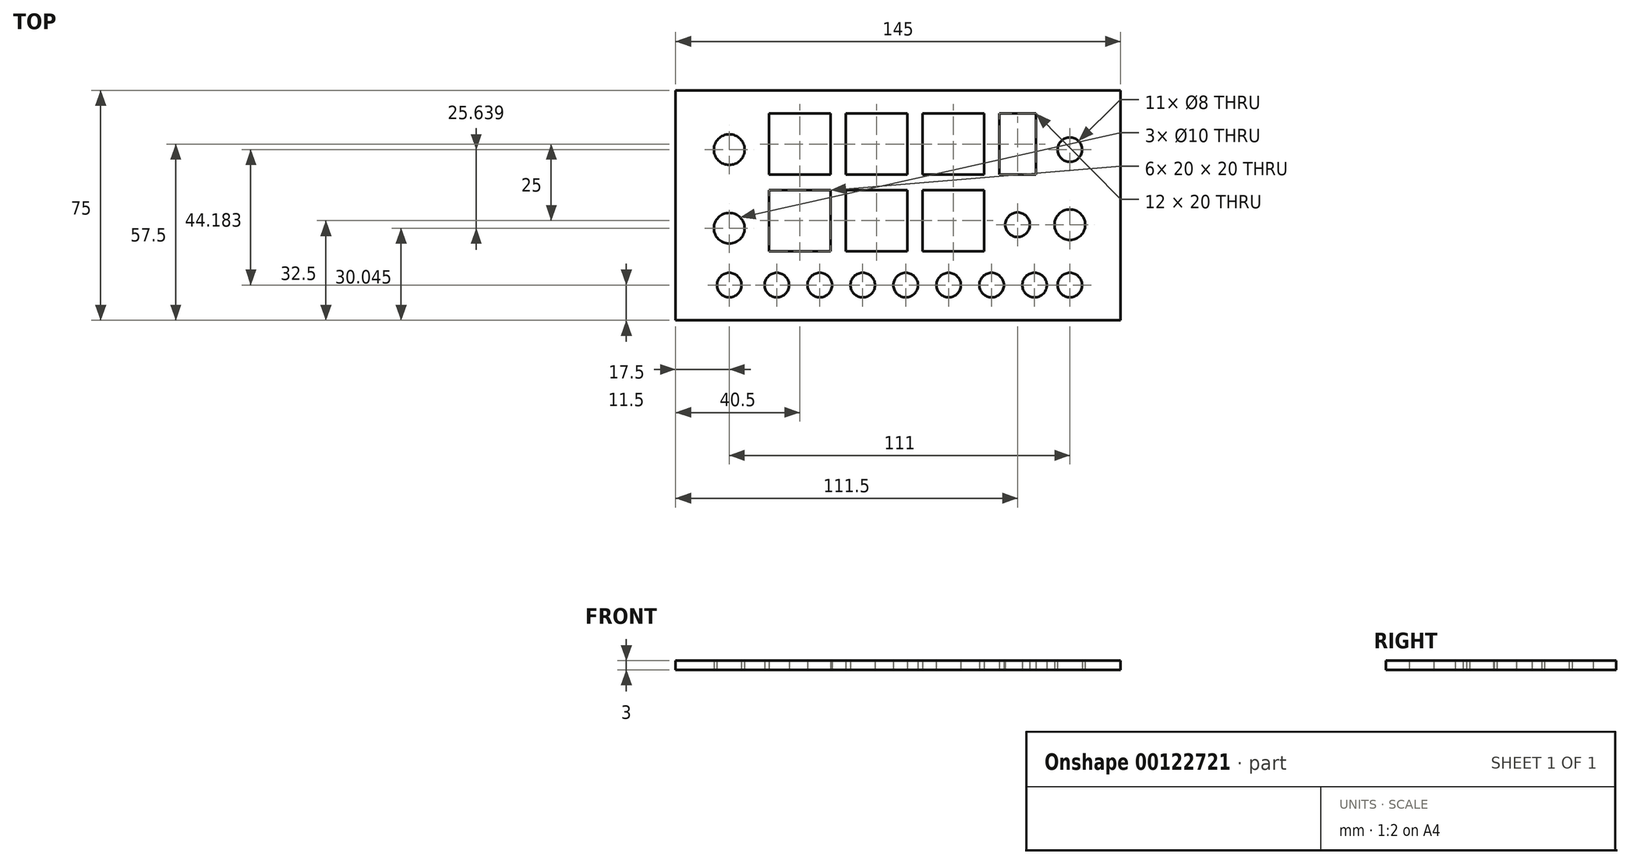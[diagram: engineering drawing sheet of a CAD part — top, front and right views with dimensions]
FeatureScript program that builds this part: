
annotation { "Feature Type Name" : "Feature", "Feature Type Description" : "" }
export const myFeature = defineFeature(function(context is Context, id is Id, definition is map)
    precondition{}
    {
        {
            var Q0;
            Q0=qCreatedBy(makeId("Top.planeOp"),FACE);
            var sketch = newSketch(context, id + "F0", { "sketchPlane" : qUnion([Q0])});
            skLineSegment(sketch, "E0.bottom", {"start": v(0, 0) * mm, "end": v(145, 0) * mm});
            skLineSegment(sketch, "E0.top", {"start": v(0, -75) * mm, "end": v(145, -75) * mm});
            skLineSegment(sketch, "E0.left", {"start": v(0, 0) * mm, "end": v(0, -75) * mm});
            skLineSegment(sketch, "E0.right", {"start": v(145, 0) * mm, "end": v(145, -75) * mm});
            skCircle(sketch, "E1", {"center": v(17.5, -19.32) * mm, "radius": 5 * mm});
            skLineSegment(sketch, "E2.bottom", {"start": v(30.5, -7.5) * mm, "end": v(50.5, -7.5) * mm});
            skLineSegment(sketch, "E2.top", {"start": v(30.5, -27.5) * mm, "end": v(50.5, -27.5) * mm});
            skLineSegment(sketch, "E2.left", {"start": v(30.5, -7.5) * mm, "end": v(30.5, -27.5) * mm});
            skLineSegment(sketch, "E2.right", {"start": v(50.5, -7.5) * mm, "end": v(50.5, -27.5) * mm});
            skLineSegment(sketch, "E3.bottom", {"start": v(55.5, -7.5) * mm, "end": v(75.5, -7.5) * mm});
            skLineSegment(sketch, "E3.top", {"start": v(55.5, -27.5) * mm, "end": v(75.5, -27.5) * mm});
            skLineSegment(sketch, "E3.left", {"start": v(55.5, -7.5) * mm, "end": v(55.5, -27.5) * mm});
            skLineSegment(sketch, "E3.right", {"start": v(75.5, -7.5) * mm, "end": v(75.5, -27.5) * mm});
            skLineSegment(sketch, "E4.bottom", {"start": v(80.5, -7.5) * mm, "end": v(100.5, -7.5) * mm});
            skLineSegment(sketch, "E4.top", {"start": v(80.5, -27.5) * mm, "end": v(100.5, -27.5) * mm});
            skLineSegment(sketch, "E4.left", {"start": v(80.5, -7.5) * mm, "end": v(80.5, -27.5) * mm});
            skLineSegment(sketch, "E4.right", {"start": v(100.5, -7.5) * mm, "end": v(100.5, -27.5) * mm});
            skLineSegment(sketch, "E5.bottom", {"start": v(105.5, -7.5) * mm, "end": v(117.5, -7.5) * mm});
            skLineSegment(sketch, "E5.top", {"start": v(105.5, -27.5) * mm, "end": v(117.5, -27.5) * mm});
            skLineSegment(sketch, "E5.left", {"start": v(105.5, -7.5) * mm, "end": v(105.5, -27.5) * mm});
            skLineSegment(sketch, "E5.right", {"start": v(117.5, -7.5) * mm, "end": v(117.5, -27.5) * mm});
            skCircle(sketch, "E6", {"center": v(128.5, -19.32) * mm, "radius": 4 * mm});
            skCircle(sketch, "E7", {"center": v(17.5, -44.96) * mm, "radius": 5 * mm});
            skLineSegment(sketch, "E8.bottom", {"start": v(30.5, -32.5) * mm, "end": v(50.5, -32.5) * mm});
            skLineSegment(sketch, "E8.top", {"start": v(30.5, -52.5) * mm, "end": v(50.5, -52.5) * mm});
            skLineSegment(sketch, "E8.left", {"start": v(30.5, -32.5) * mm, "end": v(30.5, -52.5) * mm});
            skLineSegment(sketch, "E8.right", {"start": v(50.5, -32.5) * mm, "end": v(50.5, -52.5) * mm});
            skLineSegment(sketch, "E9.bottom", {"start": v(55.5, -32.5) * mm, "end": v(75.5, -32.5) * mm});
            skLineSegment(sketch, "E9.top", {"start": v(55.5, -52.5) * mm, "end": v(75.5, -52.5) * mm});
            skLineSegment(sketch, "E9.left", {"start": v(55.5, -32.5) * mm, "end": v(55.5, -52.5) * mm});
            skLineSegment(sketch, "E9.right", {"start": v(75.5, -32.5) * mm, "end": v(75.5, -52.5) * mm});
            skLineSegment(sketch, "E10.bottom", {"start": v(80.5, -32.5) * mm, "end": v(100.5, -32.5) * mm});
            skLineSegment(sketch, "E10.top", {"start": v(80.5, -52.5) * mm, "end": v(100.5, -52.5) * mm});
            skLineSegment(sketch, "E10.left", {"start": v(80.5, -32.5) * mm, "end": v(80.5, -52.5) * mm});
            skLineSegment(sketch, "E10.right", {"start": v(100.5, -32.5) * mm, "end": v(100.5, -52.5) * mm});
            skCircle(sketch, "E11", {"center": v(17.5, -63.5) * mm, "radius": 4 * mm});
            skCircle(sketch, "E12", {"center": v(33, -63.5) * mm, "radius": 4 * mm});
            skCircle(sketch, "E13", {"center": v(47, -63.5) * mm, "radius": 4 * mm});
            skCircle(sketch, "E14", {"center": v(61, -63.5) * mm, "radius": 4 * mm});
            skCircle(sketch, "E15", {"center": v(75, -63.5) * mm, "radius": 4 * mm});
            skCircle(sketch, "E16", {"center": v(89, -63.5) * mm, "radius": 4 * mm});
            skCircle(sketch, "E17", {"center": v(103, -63.5) * mm, "radius": 4 * mm});
            skCircle(sketch, "E18", {"center": v(128.5, -63.5) * mm, "radius": 4 * mm});
            skCircle(sketch, "E19", {"center": v(117, -63.5) * mm, "radius": 4 * mm});
            skCircle(sketch, "E20", {"center": v(111.46, -43.8) * mm, "radius": 4 * mm});
            skCircle(sketch, "E21", {"center": v(128.5, -43.8) * mm, "radius": 5 * mm});
            skSolve(sketch);
        }
        {
            var Q0;
            {var subQ5=sQuery(id+"F0.wireOp",EDGE,"E0.bottom");Q0=makeQuery(id+"F0.imprint","IMPRINT",FACE,{"disambiguationData":[TD([[makeQuery(id+"F0.imprint","IMPRINT",EDGE,{"derivedFrom":subQ5}),-1.0]])]});}
            extrude(context, id + "F1", {"entities" : qUnion([Q0]), "depth" : 3 * mm});
        }
        {
            var Q0;
            Q0=makeQuery(id+"F0.imprint","IMPRINT",FACE,{"disambiguationData":[TD([[makeQuery(id+"F0.imprint","IMPRINT",EDGE,{"derivedFrom":sQuery(id+"F0.wireOp",EDGE,"E0.bottom")}),-1.0]])]});
            extrude(context, id + "F2", {"entities" : qUnion([Q0]), "oppositeDirection" : true, "depth" : 1 * mm});
        }
        {
            var Q0;
            Q0=makeQuery(id+"F2.opExtrude","SWEPT_BODY",BODY,{"disambiguationData":[OSD([sQuery(id+"F0.wireOp",EDGE,"E0.bottom"),sQuery(id+"F0.wireOp",EDGE,"E0.top"),sQuery(id+"F0.wireOp",EDGE,"E0.left"),sQuery(id+"F0.wireOp",EDGE,"E0.right"),sQuery(id+"F0.wireOp",EDGE,"E1"),sQuery(id+"F0.wireOp",EDGE,"E2.bottom"),sQuery(id+"F0.wireOp",EDGE,"E2.top"),sQuery(id+"F0.wireOp",EDGE,"E2.left"),sQuery(id+"F0.wireOp",EDGE,"E2.right"),sQuery(id+"F0.wireOp",EDGE,"E3.bottom"),sQuery(id+"F0.wireOp",EDGE,"E3.top"),sQuery(id+"F0.wireOp",EDGE,"E3.left"),sQuery(id+"F0.wireOp",EDGE,"E3.right"),sQuery(id+"F0.wireOp",EDGE,"E4.bottom"),sQuery(id+"F0.wireOp",EDGE,"E4.top"),sQuery(id+"F0.wireOp",EDGE,"E4.left"),sQuery(id+"F0.wireOp",EDGE,"E4.right"),sQuery(id+"F0.wireOp",EDGE,"E5.bottom"),sQuery(id+"F0.wireOp",EDGE,"E5.top"),sQuery(id+"F0.wireOp",EDGE,"E5.left"),sQuery(id+"F0.wireOp",EDGE,"E5.right"),sQuery(id+"F0.wireOp",EDGE,"E6"),sQuery(id+"F0.wireOp",EDGE,"E7"),sQuery(id+"F0.wireOp",EDGE,"E8.bottom"),sQuery(id+"F0.wireOp",EDGE,"E8.top"),sQuery(id+"F0.wireOp",EDGE,"E8.left"),sQuery(id+"F0.wireOp",EDGE,"E8.right"),sQuery(id+"F0.wireOp",EDGE,"E9.bottom"),sQuery(id+"F0.wireOp",EDGE,"E9.top"),sQuery(id+"F0.wireOp",EDGE,"E9.left"),sQuery(id+"F0.wireOp",EDGE,"E9.right"),sQuery(id+"F0.wireOp",EDGE,"E10.bottom"),sQuery(id+"F0.wireOp",EDGE,"E10.top"),sQuery(id+"F0.wireOp",EDGE,"E10.left"),sQuery(id+"F0.wireOp",EDGE,"E10.right"),sQuery(id+"F0.wireOp",EDGE,"E11"),sQuery(id+"F0.wireOp",EDGE,"E12"),sQuery(id+"F0.wireOp",EDGE,"E13"),sQuery(id+"F0.wireOp",EDGE,"E14"),sQuery(id+"F0.wireOp",EDGE,"E15"),sQuery(id+"F0.wireOp",EDGE,"E16"),sQuery(id+"F0.wireOp",EDGE,"E17"),sQuery(id+"F0.wireOp",EDGE,"E18"),sQuery(id+"F0.wireOp",EDGE,"E19"),sQuery(id+"F0.wireOp",EDGE,"E20"),sQuery(id+"F0.wireOp",EDGE,"E21")])]});
            deleteBodies(context, id + "F3", {"entities" : qUnion([Q0])});
        }
    });
